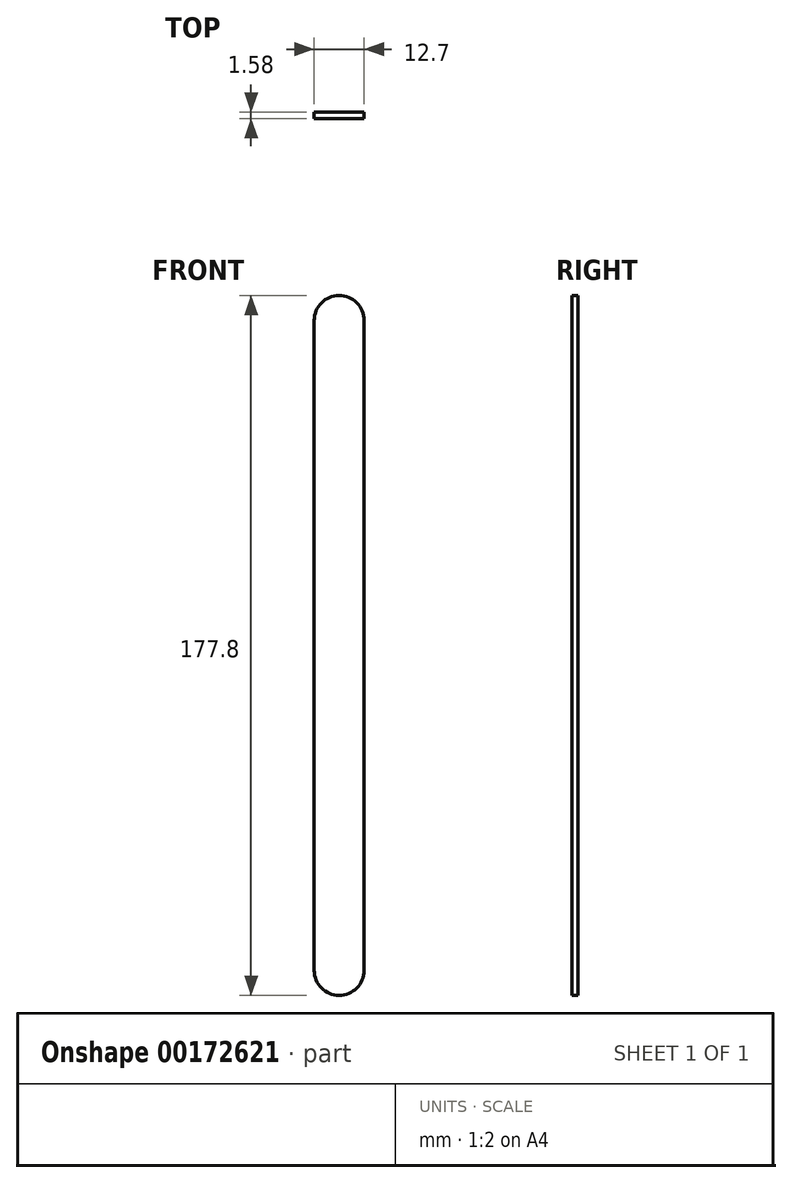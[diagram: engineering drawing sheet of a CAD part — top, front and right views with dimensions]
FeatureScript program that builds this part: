
annotation { "Feature Type Name" : "Feature", "Feature Type Description" : "" }
export const myFeature = defineFeature(function(context is Context, id is Id, definition is map)
    precondition{}
    {
        {
            var Q0;
            Q0=qCreatedBy(makeId("Front.planeOp"),FACE);
            var sketch = newSketch(context, id + "F0", { "sketchPlane" : qUnion([Q0])});
            skLineSegment(sketch, "E0.bottom", {"start": v(-0.2, 88.9) * mm, "end": v(-0.2, 88.9) * mm});
            skLineSegment(sketch, "E0.top", {"start": v(-0.2, -88.9) * mm, "end": v(-0.2, -88.9) * mm});
            skLineSegment(sketch, "E0.left", {"start": v(-6.55, 82.55) * mm, "end": v(-6.55, -82.55) * mm});
            skLineSegment(sketch, "E0.right", {"start": v(6.15, 82.55) * mm, "end": v(6.15, -82.55) * mm});
            skPoint(sketch, "E1.visualSharp", {"position": v(-6.55, 88.9) * mm});
            skArc(sketch, "E1.filletArc", {"start": v(-0.2, 88.9) * mm, "mid": v(-4.69, 87.04) * mm, "end": v(-6.55, 82.55) * mm});
            skPoint(sketch, "E2.visualSharp", {"position": v(6.15, 88.9) * mm});
            skArc(sketch, "E2.filletArc", {"start": v(6.15, 82.55) * mm, "mid": v(4.3, 87.04) * mm, "end": v(-0.2, 88.9) * mm});
            skPoint(sketch, "E3.visualSharp", {"position": v(-6.55, -88.9) * mm});
            skArc(sketch, "E3.filletArc", {"start": v(-6.55, -82.55) * mm, "mid": v(-4.69, -87.04) * mm, "end": v(-0.2, -88.9) * mm});
            skPoint(sketch, "E4.visualSharp", {"position": v(6.15, -88.9) * mm});
            skArc(sketch, "E4.filletArc", {"start": v(-0.2, -88.9) * mm, "mid": v(4.3, -87.04) * mm, "end": v(6.15, -82.55) * mm});
            skSolve(sketch);
        }
        {
            var Q0;
            Q0 = qSketchRegion(id + "F0", true);
            extrude(context, id + "F1", {"entities" : qUnion([Q0]), "endBound" : BoundingType.SYMMETRIC, "depth" : 1.59 * mm});
        }
    });
